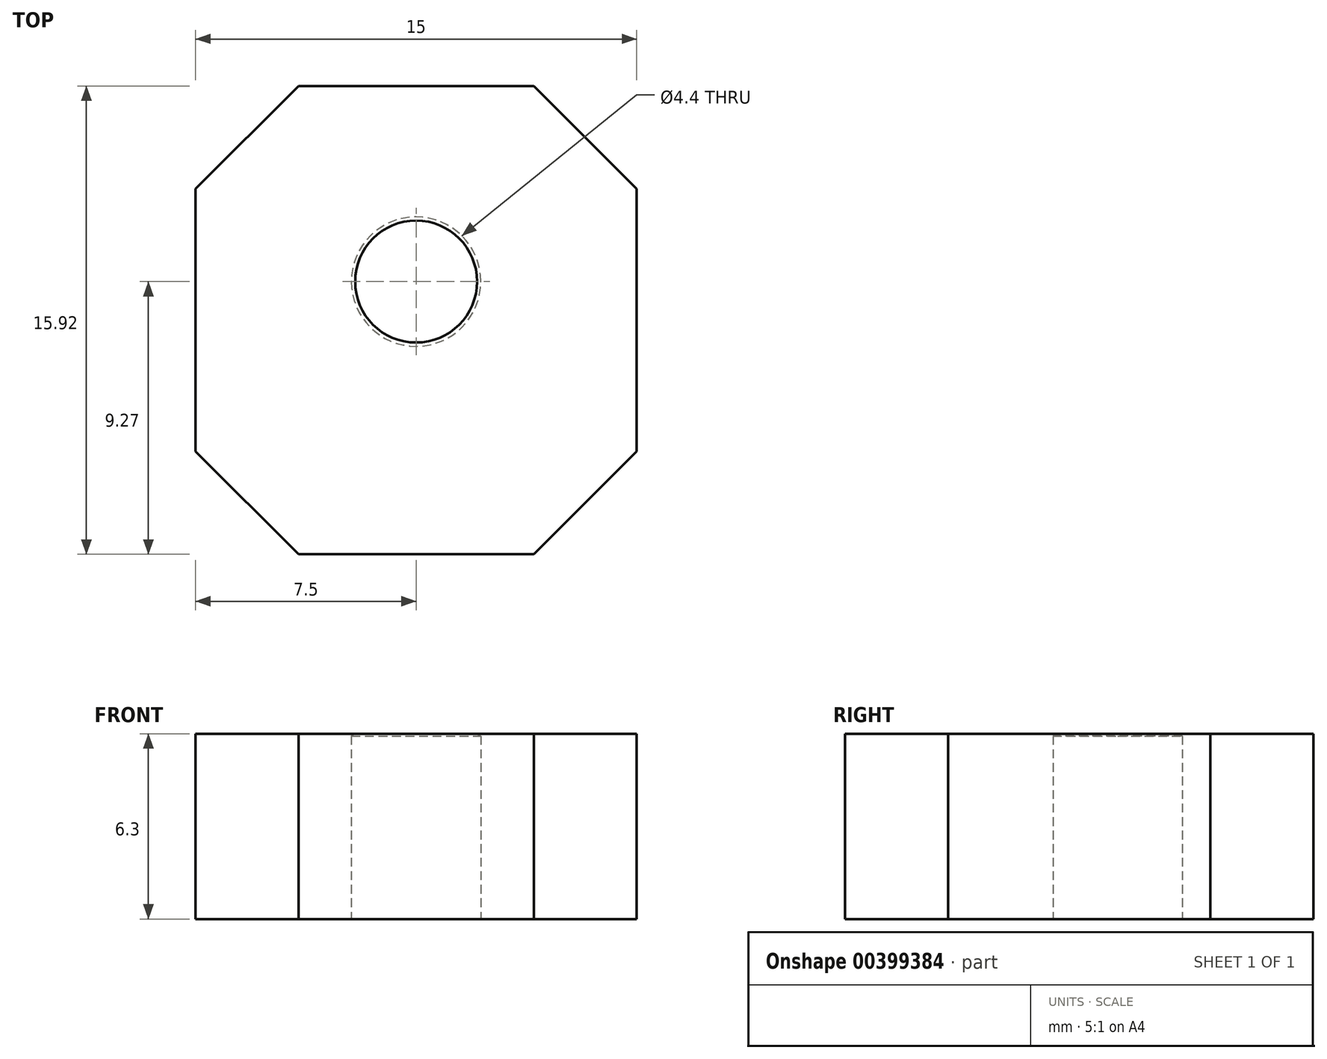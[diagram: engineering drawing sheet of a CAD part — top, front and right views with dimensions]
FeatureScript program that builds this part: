
annotation { "Feature Type Name" : "Feature", "Feature Type Description" : "" }
export const myFeature = defineFeature(function(context is Context, id is Id, definition is map)
    precondition{}
    {
        {
            var Q0;
            Q0=qCreatedBy(makeId("Top.planeOp"),FACE);
            var sketch = newSketch(context, id + "F0", { "sketchPlane" : qUnion([Q0])});
            skLineSegment(sketch, "E0.bottom", {"start": v(-4, 8.42) * mm, "end": v(4, 8.42) * mm});
            skLineSegment(sketch, "E0.top", {"start": v(-4, -7.5) * mm, "end": v(4, -7.5) * mm});
            skLineSegment(sketch, "E0.left", {"start": v(-7.5, 4.92) * mm, "end": v(-7.5, -4) * mm});
            skLineSegment(sketch, "E0.right", {"start": v(7.5, 4.92) * mm, "end": v(7.5, -4) * mm});
            skLineSegment(sketch, "E1", {"start": v(-7.5, 4.92) * mm, "end": v(-4, 8.42) * mm});
            skPoint(sketch, "E2.orphan", {"position": v(-7.5, 8.42) * mm});
            skLineSegment(sketch, "E3", {"start": v(4, 8.42) * mm, "end": v(7.5, 4.92) * mm});
            skLineSegment(sketch, "E4", {"start": v(7.5, -4) * mm, "end": v(4, -7.5) * mm});
            skLineSegment(sketch, "E5", {"start": v(-4, -7.5) * mm, "end": v(-7.5, -4) * mm});
            skPoint(sketch, "E6.orphan", {"position": v(-7.5, -7.5) * mm});
            skPoint(sketch, "E7.orphan", {"position": v(7.5, -7.5) * mm});
            skPoint(sketch, "E8.orphan", {"position": v(7.5, 8.42) * mm});
            skSolve(sketch);
        }
        {
            var Q0;
            Q0=makeQuery(id+"F0.imprint","IMPRINT",FACE,{"disambiguationData":[TD([[makeQuery(id+"F0.imprint","IMPRINT",EDGE,{"derivedFrom":sQuery(id+"F0.wireOp",EDGE,"E0.bottom")}),-1.0]])]});
            extrude(context, id + "F1", {"entities" : qUnion([Q0]), "depth" : 6.3 * mm});
        }
        {
            var Q0;
            Q0=makeQuery(id+"F1.opExtrude","CAP_FACE",FACE,{"disambiguationData":[OSD([sQuery(id+"F0.wireOp",EDGE,"E0.bottom"),sQuery(id+"F0.wireOp",EDGE,"E0.top"),sQuery(id+"F0.wireOp",EDGE,"E0.left"),sQuery(id+"F0.wireOp",EDGE,"E0.right")])],"isStart":true});
            var sketch = newSketch(context, id + "F2", { "sketchPlane" : qUnion([Q0])});
            skPoint(sketch, "E9", {"position": v(0, -1.77) * mm});
            skSolve(sketch);
        }
        {
            var Q0;
            Q0=sQuery(id+"F2.wireOp",VERTEX,"E9");
            var Q1;
            Q1=makeQuery(id+"F1.opExtrude","SWEPT_BODY",BODY,{"disambiguationData":[OSD([sQuery(id+"F0.wireOp",EDGE,"E0.bottom"),sQuery(id+"F0.wireOp",EDGE,"E0.top"),sQuery(id+"F0.wireOp",EDGE,"E0.left"),sQuery(id+"F0.wireOp",EDGE,"E0.right")])]});
            hole(context, id + "F3", {"style" : HoleStyle.SIMPLE, "endStyle" : HoleEndStyle.BLIND, "standardTappedOrClearance" : lookupTablePath({ "standard" : "ISO", "fit" : "Normal", "size" : "M4", "type" : "Clearance" }), "standardBlindInLast" : lookupTablePath({ "fit" : "Standard", "standard" : "ISO", "size" : "M4", "type" : "Clearance" }), "holeDiameter" : 4.4 * mm, "holeDepth" : 6.22 * mm, "isTappedThrough" : true, "tappedDepth" : 3.97 * mm, "tapClearance" : 3, "locations" : qUnion([Q0]), "scope" : qUnion([Q1])});
        }
    });
